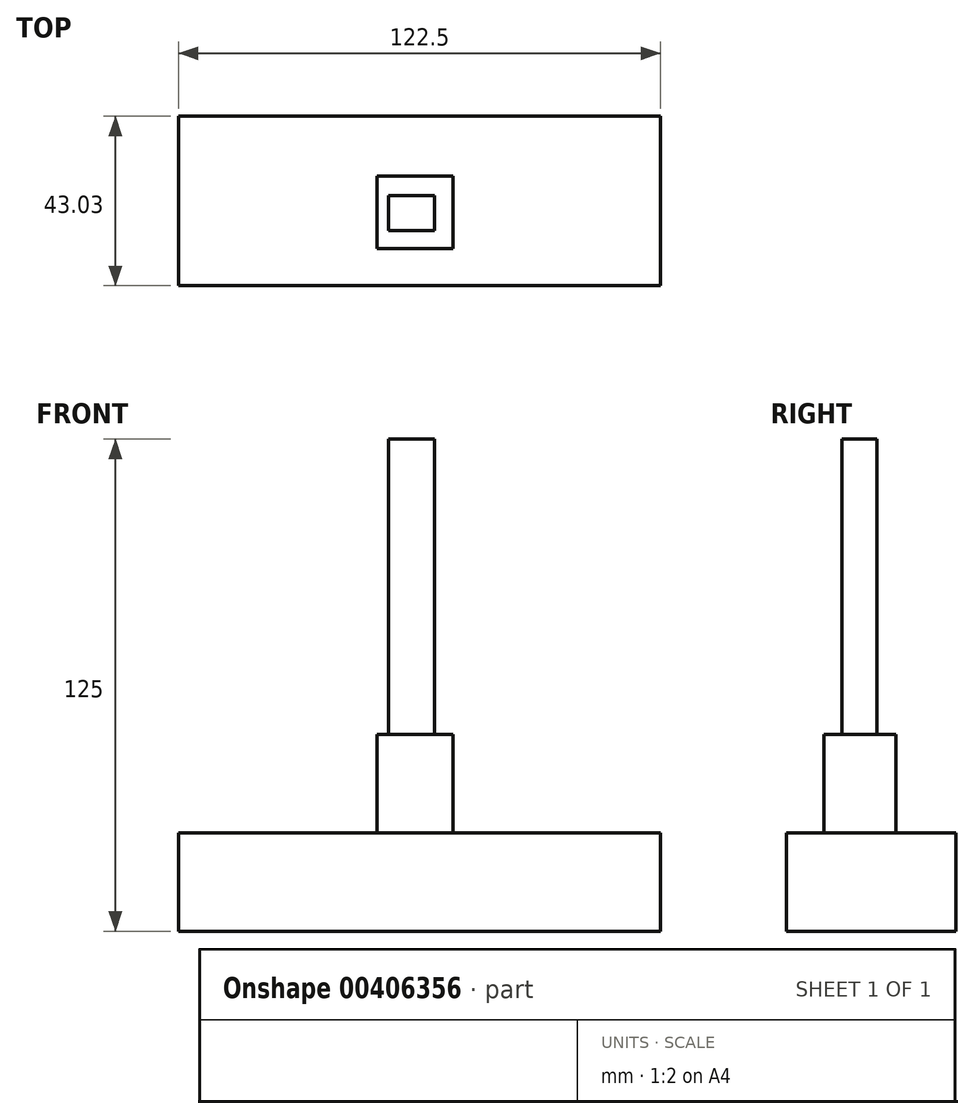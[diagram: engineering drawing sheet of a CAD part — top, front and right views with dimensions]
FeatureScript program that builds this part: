
annotation { "Feature Type Name" : "Feature", "Feature Type Description" : "" }
export const myFeature = defineFeature(function(context is Context, id is Id, definition is map)
    precondition{}
    {
        {
            var Q0;
            Q0=qCreatedBy(makeId("Top.planeOp"),FACE);
            var sketch = newSketch(context, id + "F0", { "sketchPlane" : qUnion([Q0])});
            skLineSegment(sketch, "E0.bottom", {"start": v(-59.39, 25.39) * mm, "end": v(63.11, 25.39) * mm});
            skLineSegment(sketch, "E0.top", {"start": v(-59.39, -17.64) * mm, "end": v(63.11, -17.64) * mm});
            skLineSegment(sketch, "E0.left", {"start": v(-59.39, 25.39) * mm, "end": v(-59.39, -17.64) * mm});
            skLineSegment(sketch, "E0.right", {"start": v(63.11, 25.39) * mm, "end": v(63.11, -17.64) * mm});
            skSolve(sketch);
        }
        {
            var Q0;
            Q0=makeQuery(id+"F0.imprint","IMPRINT",FACE,{"disambiguationData":[TD([[makeQuery(id+"F0.imprint","IMPRINT",EDGE,{"derivedFrom":sQuery(id+"F0.wireOp",EDGE,"E0.bottom")}),-1.0]])]});
            extrude(context, id + "F1", {"entities" : qUnion([Q0]), "depth" : 25 * mm});
        }
        {
            var Q0;
            Q0=makeQuery(id+"F1.opExtrude","CAP_FACE",FACE,{"disambiguationData":[OSD([sQuery(id+"F0.wireOp",EDGE,"E0.bottom"),sQuery(id+"F0.wireOp",EDGE,"E0.top"),sQuery(id+"F0.wireOp",EDGE,"E0.left"),sQuery(id+"F0.wireOp",EDGE,"E0.right")])],"isStart":false});
            var sketch = newSketch(context, id + "F2", { "sketchPlane" : qUnion([Q0])});
            skLineSegment(sketch, "E1.bottom", {"start": v(-8.9, 10.18) * mm, "end": v(10.33, 10.18) * mm});
            skLineSegment(sketch, "E1.top", {"start": v(-8.9, -8.18) * mm, "end": v(10.33, -8.18) * mm});
            skLineSegment(sketch, "E1.left", {"start": v(-8.9, 10.18) * mm, "end": v(-8.9, -8.18) * mm});
            skLineSegment(sketch, "E1.right", {"start": v(10.33, 10.18) * mm, "end": v(10.33, -8.18) * mm});
            skSolve(sketch);
        }
        {
            var Q0;
            Q0=makeQuery(id+"F2.imprint","IMPRINT",FACE,{"disambiguationData":[TD([[makeQuery(id+"F2.imprint","IMPRINT",EDGE,{"derivedFrom":sQuery(id+"F2.wireOp",EDGE,"E1.bottom")}),-1.0]])]});
            extrude(context, id + "F3", {"entities" : qUnion([Q0]), "operationType" : NewBodyOperationType.ADD, "depth" : 25 * mm});
        }
        {
            var Q0;
            Q0=makeQuery(id+"F3.opExtrude","SWEPT_FACE",FACE,{"disambiguationData":[OSD([sQuery(id+"F2.wireOp",EDGE,"E1.left")])]});
            var sketch = newSketch(context, id + "F4", { "sketchPlane" : qUnion([Q0])});
            skCircle(sketch, "E2", {"center": v(0, 39.45) * mm, "radius": 6.41 * mm});
            skSolve(sketch);
        }
        {
            var Q0;
            Q0=makeQuery(id+"F3.opExtrude","CAP_FACE",FACE,{"disambiguationData":[OSD([sQuery(id+"F2.wireOp",EDGE,"E1.bottom"),sQuery(id+"F2.wireOp",EDGE,"E1.top"),sQuery(id+"F2.wireOp",EDGE,"E1.left"),sQuery(id+"F2.wireOp",EDGE,"E1.right")])],"isStart":false});
            var sketch = newSketch(context, id + "F5", { "sketchPlane" : qUnion([Q0])});
            skLineSegment(sketch, "E3.bottom", {"start": v(-6.02, 5.3) * mm, "end": v(5.74, 5.3) * mm});
            skLineSegment(sketch, "E3.top", {"start": v(-6.02, -3.59) * mm, "end": v(5.74, -3.59) * mm});
            skLineSegment(sketch, "E3.left", {"start": v(-6.02, 5.3) * mm, "end": v(-6.02, -3.59) * mm});
            skLineSegment(sketch, "E3.right", {"start": v(5.74, 5.3) * mm, "end": v(5.74, -3.59) * mm});
            skSolve(sketch);
        }
        {
            var Q0;
            Q0=makeQuery(id+"F5.imprint","IMPRINT",FACE,{"disambiguationData":[TD([[makeQuery(id+"F5.imprint","IMPRINT",EDGE,{"derivedFrom":sQuery(id+"F5.wireOp",EDGE,"E3.bottom")}),-1.0]])]});
            extrude(context, id + "F6", {"entities" : qUnion([Q0]), "operationType" : NewBodyOperationType.ADD, "depth" : 75 * mm});
        }
        {
            var Q0;
            Q0=sQuery(id+"F4.wireOp",EDGE,"E2");
            var Q1;
            Q1=makeQuery(id+"F6.opExtrude","CAP_EDGE",EDGE,{"disambiguationData":[OSD([sQuery(id+"F5.wireOp",EDGE,"E3.left")])],"isStart":false});
            revolve(context, id + "F7", {"bodyType" : ToolBodyType.SURFACE, "surfaceEntities" : qUnion([Q0]), "axis" : qUnion([Q1]), "revolveType" : RevolveType.FULL});
        }
    });
